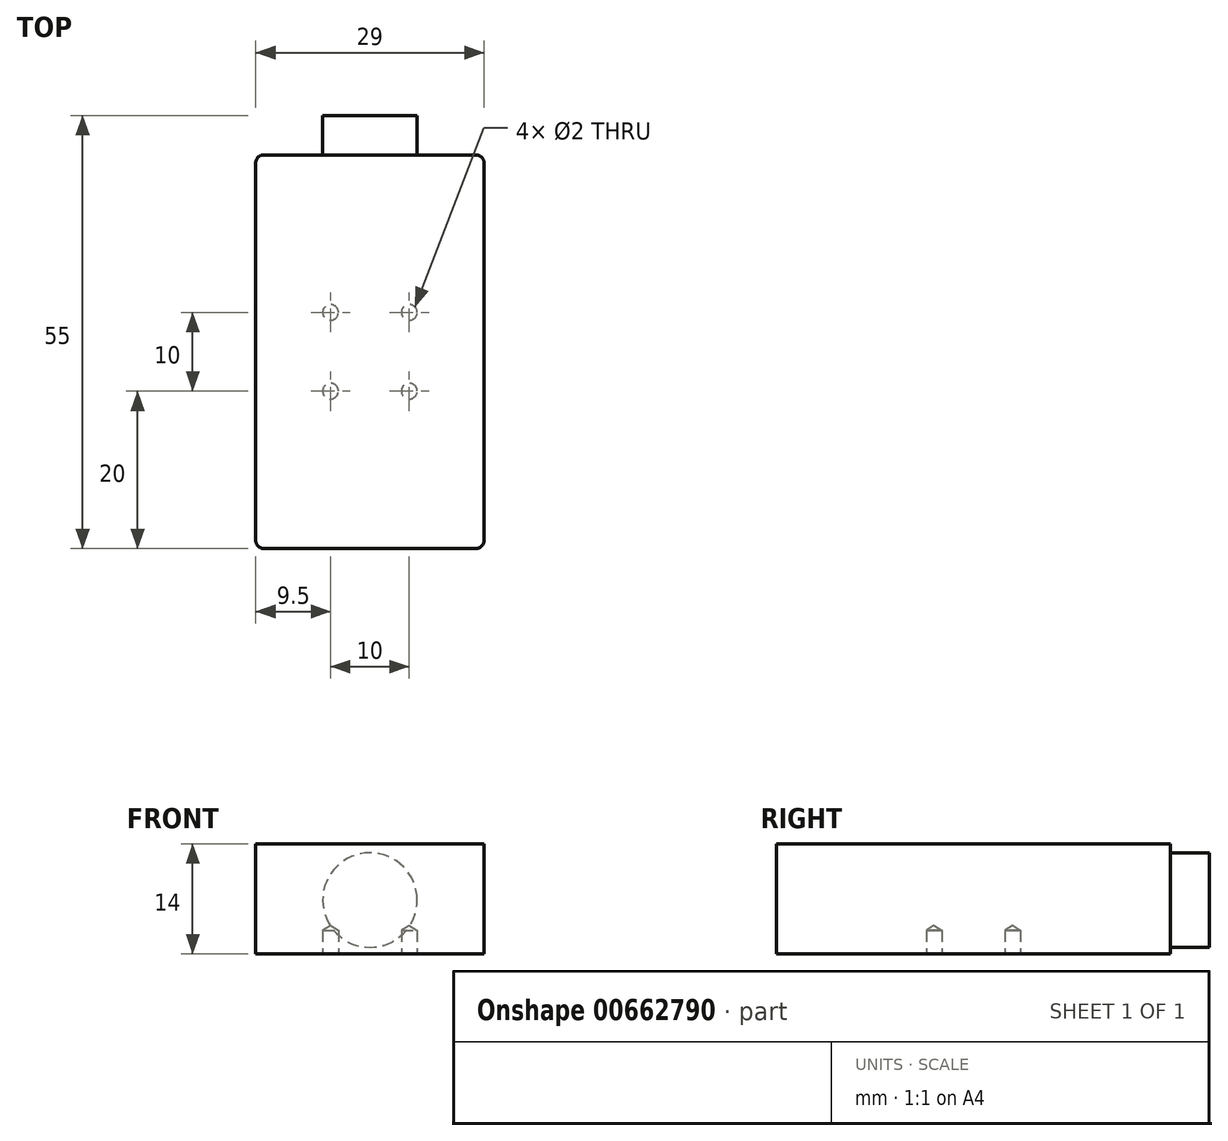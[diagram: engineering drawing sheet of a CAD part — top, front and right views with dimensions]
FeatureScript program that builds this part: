
annotation { "Feature Type Name" : "Feature", "Feature Type Description" : "" }
export const myFeature = defineFeature(function(context is Context, id is Id, definition is map)
    precondition{}
    {
        {
            var Q0;
            Q0=qCreatedBy(makeId("Top.planeOp"),FACE);
            var sketch = newSketch(context, id + "F0", { "sketchPlane" : qUnion([Q0])});
            skLineSegment(sketch, "E0.bottom", {"start": v(14.5, 25) * mm, "end": v(-14.5, 25) * mm});
            skLineSegment(sketch, "E0.top", {"start": v(14.5, -25) * mm, "end": v(-14.5, -25) * mm});
            skLineSegment(sketch, "E0.left", {"start": v(14.5, 25) * mm, "end": v(14.5, -25) * mm});
            skLineSegment(sketch, "E0.right", {"start": v(-14.5, 25) * mm, "end": v(-14.5, -25) * mm});
            skPoint(sketch, "E0.middle", {"position": v(0, 0) * mm});
            skLineSegment(sketch, "E1.bottom", {"start": v(5, 5) * mm, "end": v(-5, 5) * mm, "construction": true});
            skLineSegment(sketch, "E1.top", {"start": v(5, -5) * mm, "end": v(-5, -5) * mm, "construction": true});
            skLineSegment(sketch, "E1.left", {"start": v(5, 5) * mm, "end": v(5, -5) * mm, "construction": true});
            skLineSegment(sketch, "E1.right", {"start": v(-5, 5) * mm, "end": v(-5, -5) * mm, "construction": true});
            skSolve(sketch);
        }
        {
            var Q0;
            Q0=qCreatedBy(makeId("Front.planeOp"),FACE);
            var sketch = newSketch(context, id + "F1", { "sketchPlane" : qUnion([Q0])});
            skLineSegment(sketch, "E2", {"start": v(0, 0) * mm, "end": v(0, 14) * mm});
            skSolve(sketch);
        }
        {
            var Q0;
            Q0=makeQuery(id+"F0.imprint","IMPRINT",FACE,{"disambiguationData":[TD([[makeQuery(id+"F0.imprint","IMPRINT",EDGE,{"derivedFrom":sQuery(id+"F0.wireOp",EDGE,"E0.bottom")}),1.0]])]});
            var Q1;
            Q1=sQuery(id+"F1.wireOp",EDGE,"E2");
            sweep(context, id + "F2", {"profiles" : qUnion([Q0]), "path" : qUnion([Q1])});
        }
        {
            var Q0;
            Q0=sQuery(id+"F0.wireOp",VERTEX,"E1.left.start");
            var Q1;
            Q1=sQuery(id+"F0.wireOp",VERTEX,"E1.right.start");
            var Q2;
            Q2=sQuery(id+"F0.wireOp",VERTEX,"E1.top.end");
            var Q3;
            Q3=sQuery(id+"F0.wireOp",VERTEX,"E1.top.start");
            var Q4;
            Q4=makeQuery(id+"F2.opSweep","SWEPT_BODY",BODY,{"disambiguationData":[OSD([sQuery(id+"F0.wireOp",EDGE,"E0.bottom"),sQuery(id+"F0.wireOp",EDGE,"E0.top"),sQuery(id+"F0.wireOp",EDGE,"E0.left"),sQuery(id+"F0.wireOp",EDGE,"E0.right"),sQuery(id+"F1.wireOp",EDGE,"E2")])]});
            hole(context, id + "F3", {"style" : HoleStyle.SIMPLE, "endStyle" : HoleEndStyle.BLIND, "oppositeDirection" : true, "holeDiameter" : 2 * mm, "majorDiameter" : 5 * mm, "holeDepth" : 3 * mm, "isTappedThrough" : true, "tappedDepth" : 12 * mm, "tapClearance" : 3, "locations" : qUnion([Q0, Q1, Q2, Q3]), "scope" : qUnion([Q4])});
        }
        {
            var Q0;
            Q0=makeQuery(id+"F2.opSweep","SWEPT_EDGE",EDGE,{"disambiguationData":[OSD([sQuery(id+"F0.wireOp",EDGE,"E0.top"),sQuery(id+"F0.wireOp",EDGE,"E0.left"),sQuery(id+"F1.wireOp",EDGE,"E2")])]});
            var Q1;
            Q1=makeQuery(id+"F2.opSweep","SWEPT_EDGE",EDGE,{"disambiguationData":[OSD([sQuery(id+"F0.wireOp",EDGE,"E0.top"),sQuery(id+"F0.wireOp",EDGE,"E0.right"),sQuery(id+"F1.wireOp",EDGE,"E2")])]});
            var Q2;
            Q2=makeQuery(id+"F2.opSweep","SWEPT_EDGE",EDGE,{"disambiguationData":[OSD([sQuery(id+"F0.wireOp",EDGE,"E0.bottom"),sQuery(id+"F0.wireOp",EDGE,"E0.left"),sQuery(id+"F1.wireOp",EDGE,"E2")])]});
            var Q3;
            Q3=makeQuery(id+"F2.opSweep","SWEPT_EDGE",EDGE,{"disambiguationData":[OSD([sQuery(id+"F0.wireOp",EDGE,"E0.bottom"),sQuery(id+"F0.wireOp",EDGE,"E0.right"),sQuery(id+"F1.wireOp",EDGE,"E2")])]});
            fillet(context, id + "F4", {"entities" : qUnion([Q0, Q1, Q2, Q3]), "radius" : 1 * mm, "allowEdgeOverflow" : false});
        }
        {
            var Q0;
            Q0=makeQuery(id+"F2.opSweep","SWEPT_FACE",FACE,{"disambiguationData":[OSD([sQuery(id+"F0.wireOp",EDGE,"E0.bottom"),sQuery(id+"F1.wireOp",EDGE,"E2")])]});
            var sketch = newSketch(context, id + "F5", { "sketchPlane" : qUnion([Q0])});
            skCircle(sketch, "E3", {"center": v(0, 6.83) * mm, "radius": 6 * mm});
            skSolve(sketch);
        }
        {
            var Q0;
            Q0 = qSketchRegion(id + "F5", true);
            extrude(context, id + "F6", {"entities" : qUnion([Q0]), "operationType" : NewBodyOperationType.ADD, "depth" : 5 * mm, "offsetDistance" : 25 * mm});
        }
    });
